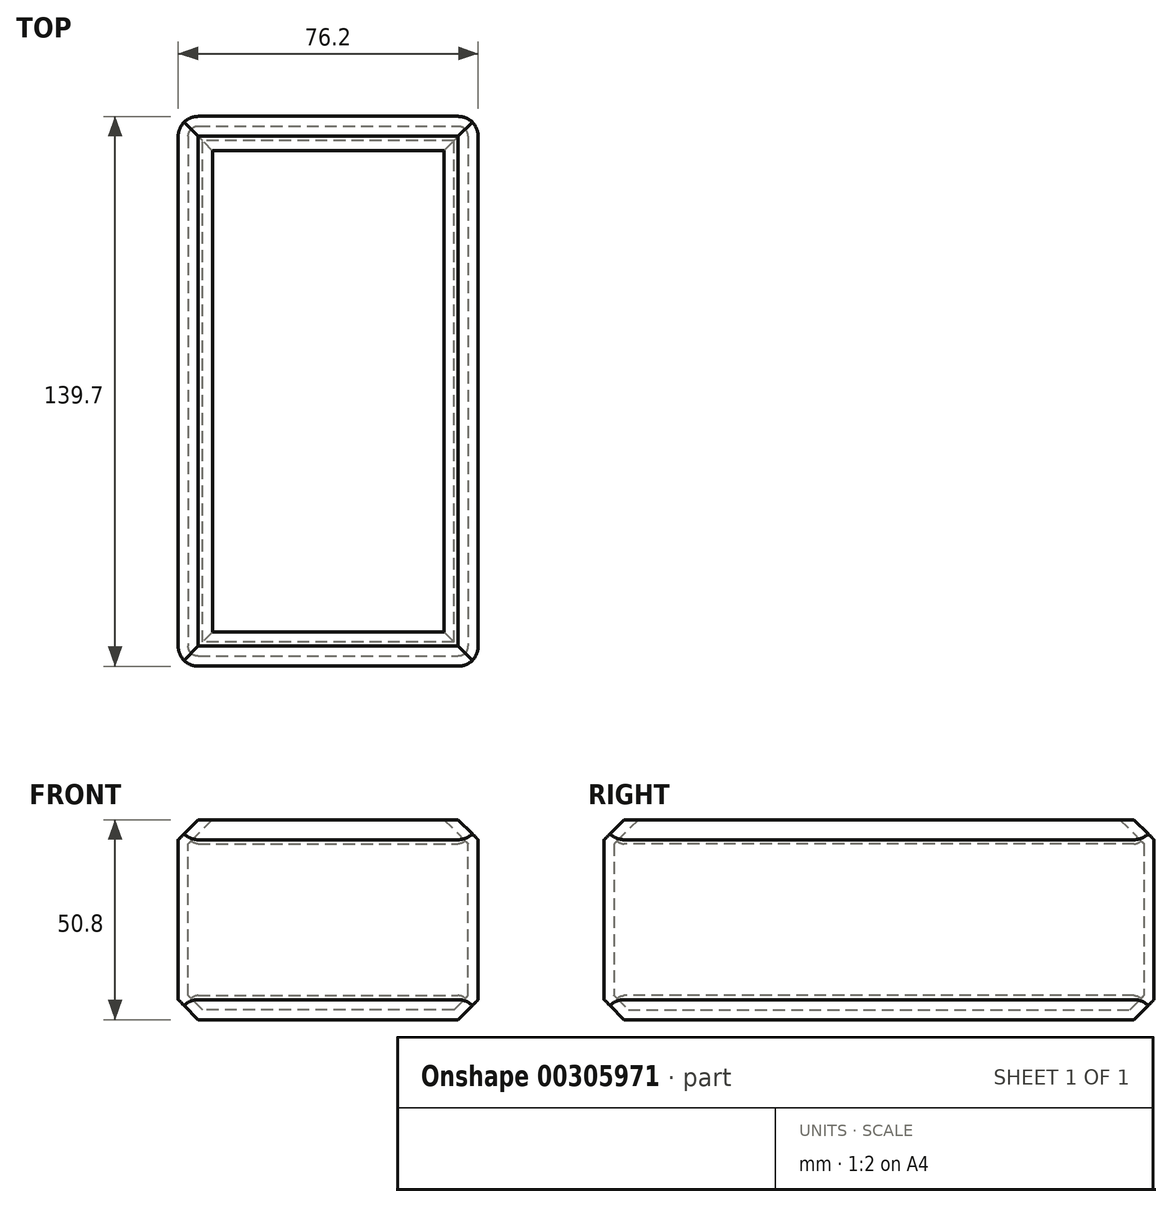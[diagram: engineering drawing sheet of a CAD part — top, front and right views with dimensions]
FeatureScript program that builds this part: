
annotation { "Feature Type Name" : "Feature", "Feature Type Description" : "" }
export const myFeature = defineFeature(function(context is Context, id is Id, definition is map)
    precondition{}
    {
        {
            var Q0;
            Q0=qCreatedBy(makeId("Top.planeOp"),FACE);
            var sketch = newSketch(context, id + "F0", { "sketchPlane" : qUnion([Q0])});
            skLineSegment(sketch, "E0.bottom", {"start": v(-41.44, 64.3) * mm, "end": v(34.76, 64.3) * mm});
            skLineSegment(sketch, "E0.top", {"start": v(-41.44, -75.4) * mm, "end": v(34.76, -75.4) * mm});
            skLineSegment(sketch, "E0.left", {"start": v(-41.44, 64.3) * mm, "end": v(-41.44, -75.4) * mm});
            skLineSegment(sketch, "E0.right", {"start": v(34.76, 64.3) * mm, "end": v(34.76, -75.4) * mm});
            skSolve(sketch);
        }
        {
            var Q0;
            Q0=makeQuery(id+"F0.imprint","IMPRINT",FACE,{"disambiguationData":[TD([[makeQuery(id+"F0.imprint","IMPRINT",EDGE,{"derivedFrom":sQuery(id+"F0.wireOp",EDGE,"E0.bottom")}),-1.0]])]});
            extrude(context, id + "F1", {"entities" : qUnion([Q0]), "oppositeDirection" : true, "depth" : 50.8 * mm});
        }
        {
            var Q0;
            Q0=makeQuery(id+"F1.opExtrude","CAP_EDGE",EDGE,{"disambiguationData":[OSD([sQuery(id+"F0.wireOp",EDGE,"E0.top")])],"isStart":true});
            var Q1;
            Q1=makeQuery(id+"F1.opExtrude","CAP_EDGE",EDGE,{"disambiguationData":[OSD([sQuery(id+"F0.wireOp",EDGE,"E0.right")])],"isStart":true});
            var Q2;
            Q2=makeQuery(id+"F1.opExtrude","CAP_EDGE",EDGE,{"disambiguationData":[OSD([sQuery(id+"F0.wireOp",EDGE,"E0.left")])],"isStart":true});
            var Q3;
            Q3=makeQuery(id+"F1.opExtrude","CAP_EDGE",EDGE,{"disambiguationData":[OSD([sQuery(id+"F0.wireOp",EDGE,"E0.bottom")])],"isStart":true});
            var Q4;
            Q4=makeQuery(id+"F1.opExtrude","CAP_EDGE",EDGE,{"disambiguationData":[OSD([sQuery(id+"F0.wireOp",EDGE,"E0.right")])],"isStart":false});
            var Q5;
            Q5=makeQuery(id+"F1.opExtrude","CAP_EDGE",EDGE,{"disambiguationData":[OSD([sQuery(id+"F0.wireOp",EDGE,"E0.top")])],"isStart":false});
            var Q6;
            Q6=makeQuery(id+"F1.opExtrude","CAP_EDGE",EDGE,{"disambiguationData":[OSD([sQuery(id+"F0.wireOp",EDGE,"E0.bottom")])],"isStart":false});
            var Q7;
            Q7=makeQuery(id+"F1.opExtrude","CAP_EDGE",EDGE,{"disambiguationData":[OSD([sQuery(id+"F0.wireOp",EDGE,"E0.left")])],"isStart":false});
            chamfer(context, id + "F2", {"entities" : qUnion([Q0, Q1, Q2, Q3, Q4, Q5, Q6, Q7]), "width" : 5.08 * mm, "tangentPropagation" : true});
        }
        {
            var Q0;
            Q0=makeQuery(id+"F1.opExtrude","SWEPT_EDGE",EDGE,{"disambiguationData":[OSD([sQuery(id+"F0.wireOp",EDGE,"E0.top"),sQuery(id+"F0.wireOp",EDGE,"E0.right")])]});
            var Q1;
            Q1=makeQuery(id+"F1.opExtrude","SWEPT_EDGE",EDGE,{"disambiguationData":[OSD([sQuery(id+"F0.wireOp",EDGE,"E0.bottom"),sQuery(id+"F0.wireOp",EDGE,"E0.right")])]});
            var Q2;
            Q2=makeQuery(id+"F1.opExtrude","SWEPT_EDGE",EDGE,{"disambiguationData":[OSD([sQuery(id+"F0.wireOp",EDGE,"E0.bottom"),sQuery(id+"F0.wireOp",EDGE,"E0.left")])]});
            var Q3;
            Q3=makeQuery(id+"F1.opExtrude","SWEPT_EDGE",EDGE,{"disambiguationData":[OSD([sQuery(id+"F0.wireOp",EDGE,"E0.top"),sQuery(id+"F0.wireOp",EDGE,"E0.left")])]});
            fillet(context, id + "F3", {"entities" : qUnion([Q0, Q1, Q2, Q3]), "radius" : 5.08 * mm, "tangentPropagation" : true, "allowEdgeOverflow" : false});
        }
        {
            var Q0;
            Q0=makeQuery(id+"F1.opExtrude","CAP_FACE",FACE,{"disambiguationData":[OSD([sQuery(id+"F0.wireOp",EDGE,"E0.bottom"),sQuery(id+"F0.wireOp",EDGE,"E0.top"),sQuery(id+"F0.wireOp",EDGE,"E0.left"),sQuery(id+"F0.wireOp",EDGE,"E0.right")])],"isStart":true});
            shell(context, id + "F4", {"entities" : qUnion([Q0]), "thickness" : 2.54 * mm});
        }
    });
